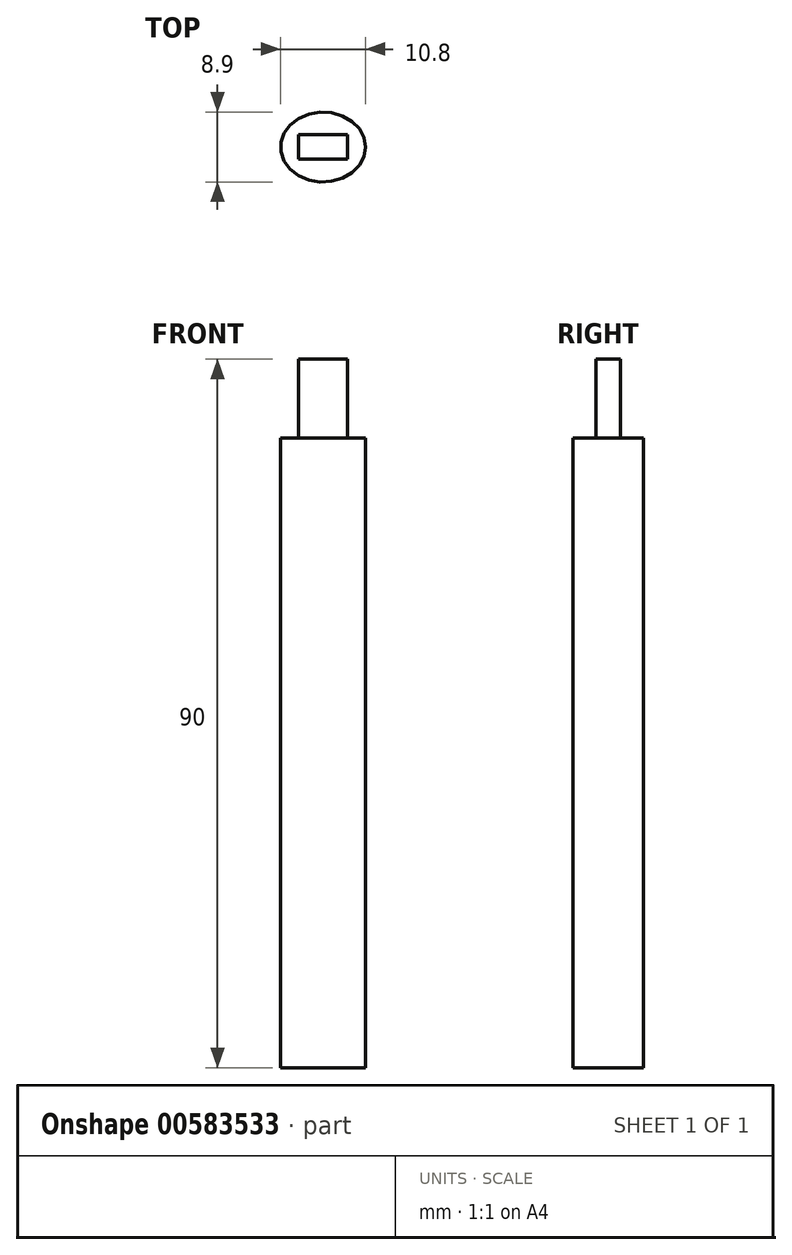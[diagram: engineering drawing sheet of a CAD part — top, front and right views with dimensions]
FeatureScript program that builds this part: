
annotation { "Feature Type Name" : "Feature", "Feature Type Description" : "" }
export const myFeature = defineFeature(function(context is Context, id is Id, definition is map)
    precondition{}
    {
        {
            var Q0;
            Q0=qCreatedBy(makeId("Top.planeOp"),FACE);
            var sketch = newSketch(context, id + "F0", { "sketchPlane" : qUnion([Q0])});
            skEllipse(sketch, "E0", {"center": v(0, 0) * mm, "majorRadius": 5.4 * mm, "minorRadius": 4.45 * mm, "majorAxis": v(1, 0)});
            skPoint(sketch, "E1", {"position": v(-5.4, 0) * mm});
            skPoint(sketch, "E2", {"position": v(0, -4.45) * mm});
            skPoint(sketch, "E3", {"position": v(5.4, 0) * mm});
            skPoint(sketch, "E4", {"position": v(0, 4.45) * mm});
            skSolve(sketch);
        }
        {
            var Q0;
            Q0=makeQuery(id+"F0.imprint","IMPRINT",FACE,{"disambiguationData":[TD([[makeQuery(id+"F0.imprint","IMPRINT",EDGE,{"derivedFrom":sQuery(id+"F0.wireOp",EDGE,"E0")}),1.0]])]});
            extrude(context, id + "F1", {"entities" : qUnion([Q0]), "depth" : 80 * mm, "offsetDistance" : 25 * mm});
        }
        {
            var Q0;
            Q0=makeQuery(id+"F1.opExtrude","CAP_FACE",FACE,{"disambiguationData":[OSD([sQuery(id+"F0.wireOp",EDGE,"E0")])],"isStart":false});
            var sketch = newSketch(context, id + "F2", { "sketchPlane" : qUnion([Q0])});
            skLineSegment(sketch, "E5.bottom", {"start": v(3.12, 1.55) * mm, "end": v(-3.12, 1.55) * mm});
            skLineSegment(sketch, "E5.top", {"start": v(3.12, -1.55) * mm, "end": v(-3.12, -1.55) * mm});
            skLineSegment(sketch, "E5.left", {"start": v(3.12, 1.55) * mm, "end": v(3.12, -1.55) * mm});
            skLineSegment(sketch, "E5.right", {"start": v(-3.12, 1.55) * mm, "end": v(-3.12, -1.55) * mm});
            skPoint(sketch, "E5.middle", {"position": v(0, 0) * mm});
            skSolve(sketch);
        }
        {
            var Q0;
            Q0=makeQuery(id+"F2.imprint","IMPRINT",FACE,{"disambiguationData":[TD([[makeQuery(id+"F2.imprint","IMPRINT",EDGE,{"derivedFrom":sQuery(id+"F2.wireOp",EDGE,"E5.bottom")}),1.0]])]});
            extrude(context, id + "F3", {"entities" : qUnion([Q0]), "operationType" : NewBodyOperationType.ADD, "depth" : 10 * mm, "offsetDistance" : 25 * mm});
        }
    });
